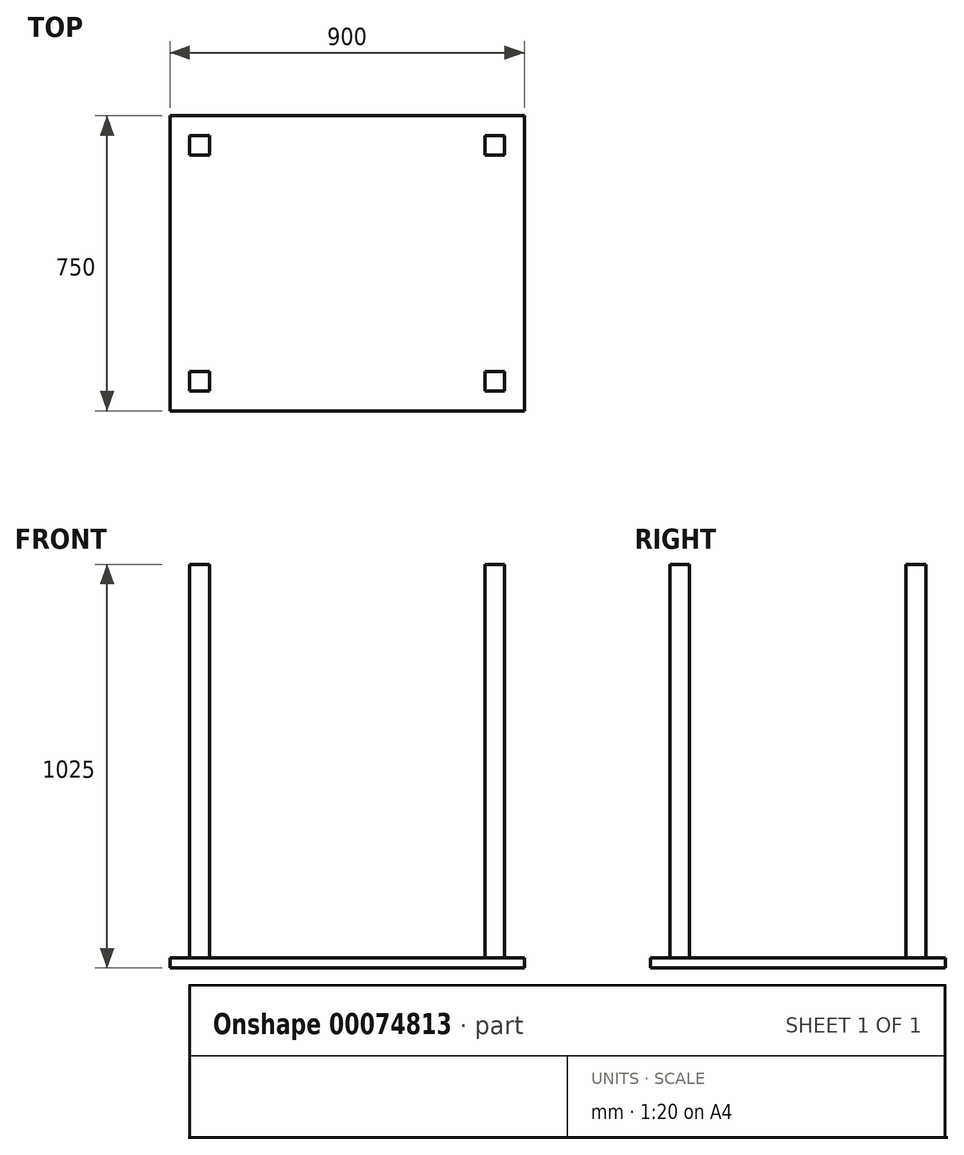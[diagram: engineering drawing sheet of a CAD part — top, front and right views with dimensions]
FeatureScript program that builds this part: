
annotation { "Feature Type Name" : "Feature", "Feature Type Description" : "" }
export const myFeature = defineFeature(function(context is Context, id is Id, definition is map)
    precondition{}
    {
        {
            var Q0;
            Q0=qCreatedBy(makeId("Top.planeOp"),FACE);
            var sketch = newSketch(context, id + "F0", { "sketchPlane" : qUnion([Q0])});
            skLineSegment(sketch, "E0.bottom", {"start": v(0, 0) * mm, "end": v(900, 0) * mm});
            skLineSegment(sketch, "E0.top", {"start": v(0, -750) * mm, "end": v(900, -750) * mm});
            skLineSegment(sketch, "E0.left", {"start": v(0, 0) * mm, "end": v(0, -750) * mm});
            skLineSegment(sketch, "E0.right", {"start": v(900, 0) * mm, "end": v(900, -750) * mm});
            skSolve(sketch);
        }
        {
            var Q0;
            Q0=qSketchRegion(id+"F0",true);
            extrude(context, id + "F1", {"entities" : qUnion([Q0]), "depth" : 25 * mm});
        }
        {
            var Q0;
            Q0=makeQuery(id+"F1.opExtrude","CAP_FACE",FACE,{"disambiguationData":[OSD([sQuery(id+"F0.wireOp",EDGE,"E0.bottom"),sQuery(id+"F0.wireOp",EDGE,"E0.top"),sQuery(id+"F0.wireOp",EDGE,"E0.left"),sQuery(id+"F0.wireOp",EDGE,"E0.right")])],"isStart":false});
            var sketch = newSketch(context, id + "F2", { "sketchPlane" : qUnion([Q0])});
            skLineSegment(sketch, "E1.bottom", {"start": v(50, -50) * mm, "end": v(100, -50) * mm});
            skLineSegment(sketch, "E1.top", {"start": v(50, -100) * mm, "end": v(100, -100) * mm});
            skLineSegment(sketch, "E1.left", {"start": v(50, -50) * mm, "end": v(50, -100) * mm});
            skLineSegment(sketch, "E1.right", {"start": v(100, -50) * mm, "end": v(100, -100) * mm});
            skLineSegment(sketch, "E2.bottom", {"start": v(50, -650) * mm, "end": v(100, -650) * mm});
            skLineSegment(sketch, "E2.top", {"start": v(50, -700) * mm, "end": v(100, -700) * mm});
            skLineSegment(sketch, "E2.left", {"start": v(50, -650) * mm, "end": v(50, -700) * mm});
            skLineSegment(sketch, "E2.right", {"start": v(100, -650) * mm, "end": v(100, -700) * mm});
            skLineSegment(sketch, "E3.bottom", {"start": v(800, -50) * mm, "end": v(850, -50) * mm});
            skLineSegment(sketch, "E3.top", {"start": v(800, -100) * mm, "end": v(850, -100) * mm});
            skLineSegment(sketch, "E3.left", {"start": v(800, -50) * mm, "end": v(800, -100) * mm});
            skLineSegment(sketch, "E3.right", {"start": v(850, -50) * mm, "end": v(850, -100) * mm});
            skLineSegment(sketch, "E4.bottom", {"start": v(800, -650) * mm, "end": v(850, -650) * mm});
            skLineSegment(sketch, "E4.top", {"start": v(800, -700) * mm, "end": v(850, -700) * mm});
            skLineSegment(sketch, "E4.left", {"start": v(800, -650) * mm, "end": v(800, -700) * mm});
            skLineSegment(sketch, "E4.right", {"start": v(850, -650) * mm, "end": v(850, -700) * mm});
            skSolve(sketch);
        }
        {
            var Q0;
            Q0=qSketchRegion(id+"F2",true);
            extrude(context, id + "F3", {"entities" : qUnion([Q0]), "operationType" : NewBodyOperationType.ADD, "depth" : 1000 * mm});
        }
    });
